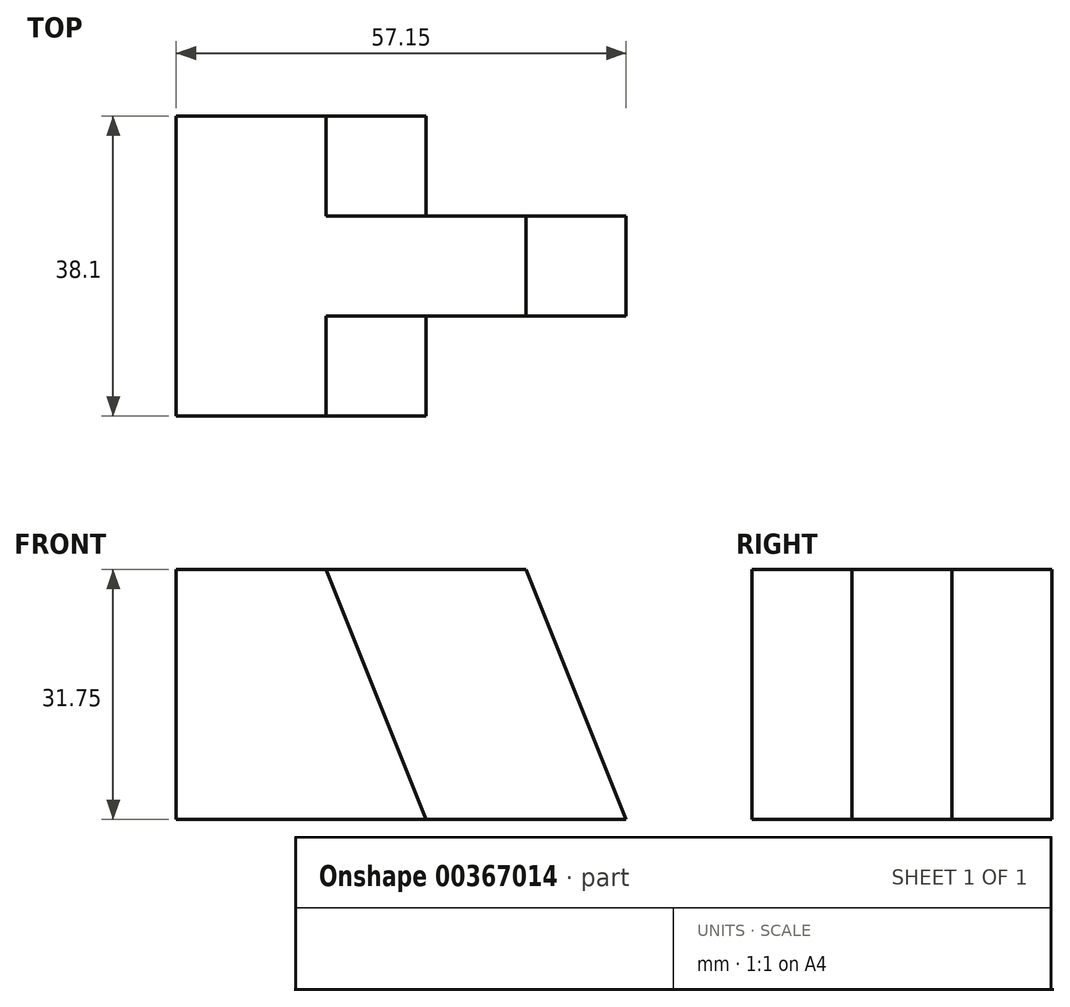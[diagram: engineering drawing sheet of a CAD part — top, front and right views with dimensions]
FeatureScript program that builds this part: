
annotation { "Feature Type Name" : "Feature", "Feature Type Description" : "" }
export const myFeature = defineFeature(function(context is Context, id is Id, definition is map)
    precondition{}
    {
        {
            var Q0;
            Q0=qCreatedBy(makeId("Top.planeOp"),FACE);
            var sketch = newSketch(context, id + "F0", { "sketchPlane" : qUnion([Q0])});
            skLineSegment(sketch, "E0", {"start": v(0, 0) * mm, "end": v(0, 38.1) * mm});
            skLineSegment(sketch, "E1", {"start": v(0, 38.1) * mm, "end": v(31.75, 38.1) * mm});
            skLineSegment(sketch, "E2", {"start": v(31.75, 38.1) * mm, "end": v(31.75, 25.4) * mm});
            skLineSegment(sketch, "E3", {"start": v(31.75, 25.4) * mm, "end": v(57.15, 25.4) * mm});
            skLineSegment(sketch, "E4", {"start": v(57.15, 25.4) * mm, "end": v(57.15, 12.7) * mm});
            skLineSegment(sketch, "E5", {"start": v(57.15, 12.7) * mm, "end": v(31.75, 12.7) * mm});
            skLineSegment(sketch, "E6", {"start": v(31.75, 12.7) * mm, "end": v(31.75, 0) * mm});
            skLineSegment(sketch, "E7", {"start": v(31.75, 0) * mm, "end": v(0, 0) * mm});
            skSolve(sketch);
        }
        {
            var Q0;
            Q0 = qSketchRegion(id + "F0", true);
            extrude(context, id + "F1", {"entities" : qUnion([Q0]), "depth" : 31.75 * mm});
        }
        {
            var Q0;
            Q0=makeQuery(id+"F1.opExtrude","SWEPT_FACE",FACE,{"disambiguationData":[OSD([sQuery(id+"F0.wireOp",EDGE,"E7")])]});
            var sketch = newSketch(context, id + "F2", { "sketchPlane" : qUnion([Q0])});
            skLineSegment(sketch, "E8", {"start": v(31.75, 0) * mm, "end": v(19.05, 31.75) * mm});
            skLineSegment(sketch, "E9", {"start": v(19.05, 31.75) * mm, "end": v(31.75, 31.75) * mm});
            skLineSegment(sketch, "E10", {"start": v(31.75, 31.75) * mm, "end": v(31.75, 0) * mm});
            skSolve(sketch);
        }
        {
            var Q0;
            Q0 = qSketchRegion(id + "F2", true);
            extrude(context, id + "F3", {"entities" : qUnion([Q0]), "operationType" : NewBodyOperationType.REMOVE, "oppositeDirection" : true, "depth" : 12.7 * mm});
        }
        {
            var Q0;
            Q0=makeQuery(id+"F1.opExtrude","SWEPT_FACE",FACE,{"disambiguationData":[OSD([sQuery(id+"F0.wireOp",EDGE,"E1")])]});
            var sketch = newSketch(context, id + "F4", { "sketchPlane" : qUnion([Q0])});
            skLineSegment(sketch, "E11", {"start": v(-31.75, 0) * mm, "end": v(-19.05, 31.75) * mm});
            skSolve(sketch);
        }
        {
            var Q0;
            {var subQ0=sQuery(id+"F4.wireOp",EDGE,"E11");Q0=makeQuery(id+"F4.imprint","IMPRINT",FACE,{"disambiguationData":[TD([[makeQuery(id+"F4.imprint","IMPRINT",EDGE,{"derivedFrom":subQ0}),1.0]])]});}
            extrude(context, id + "F5", {"entities" : qUnion([Q0]), "operationType" : NewBodyOperationType.REMOVE, "oppositeDirection" : true, "depth" : 12.7 * mm});
        }
        {
            var Q0;
            Q0=makeQuery(id+"F3.boolean.opBoolean","MERGE",FACE,{"derivedFrom":[makeQuery(id+"F1.opExtrude","SWEPT_FACE",FACE,{"disambiguationData":[OSD([sQuery(id+"F0.wireOp",EDGE,"E5")])]}),makeQuery(id+"F3.opExtrude","CAP_FACE",FACE,{"disambiguationData":[OSD([sQuery(id+"F2.wireOp",EDGE,"E8"),sQuery(id+"F2.wireOp",EDGE,"E9"),sQuery(id+"F2.wireOp",EDGE,"E10")])],"isStart":false})]});
            var sketch = newSketch(context, id + "F6", { "sketchPlane" : qUnion([Q0])});
            skLineSegment(sketch, "E12", {"start": v(57.15, 0) * mm, "end": v(44.45, 31.75) * mm});
            skSolve(sketch);
        }
        {
            var Q0;
            {var subQ0=sQuery(id+"F6.wireOp",EDGE,"E12");Q0=makeQuery(id+"F6.imprint","IMPRINT",FACE,{"disambiguationData":[TD([[makeQuery(id+"F6.imprint","IMPRINT",EDGE,{"derivedFrom":subQ0}),-1.0]])]});}
            extrude(context, id + "F7", {"entities" : qUnion([Q0]), "operationType" : NewBodyOperationType.REMOVE, "oppositeDirection" : true, "depth" : 25.4 * mm});
        }
    });
